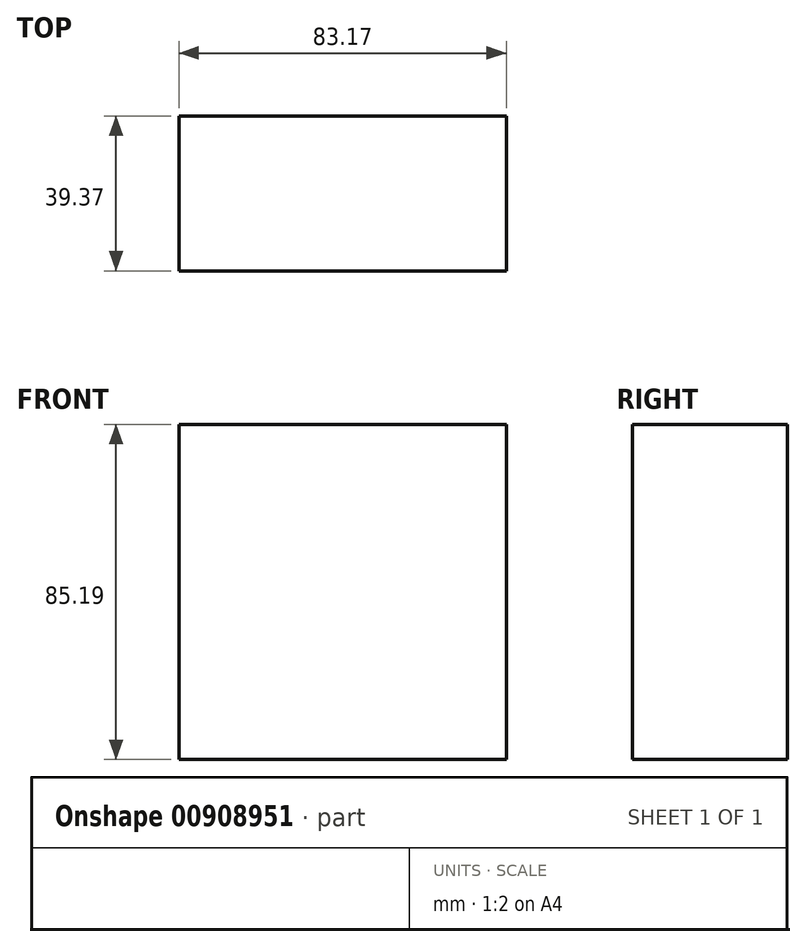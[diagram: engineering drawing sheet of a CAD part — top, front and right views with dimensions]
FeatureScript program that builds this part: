
annotation { "Feature Type Name" : "Feature", "Feature Type Description" : "" }
export const myFeature = defineFeature(function(context is Context, id is Id, definition is map)
    precondition{}
    {
        {
            var Q0;
            Q0=qCreatedBy(makeId("Front.planeOp"),FACE);
            var sketch = newSketch(context, id + "F0", { "sketchPlane" : qUnion([Q0])});
            skLineSegment(sketch, "E0.bottom", {"start": v(-42.1, 43.48) * mm, "end": v(41.08, 43.48) * mm});
            skLineSegment(sketch, "E0.top", {"start": v(-42.1, -41.71) * mm, "end": v(41.08, -41.71) * mm});
            skLineSegment(sketch, "E0.left", {"start": v(-42.1, 43.48) * mm, "end": v(-42.1, -41.71) * mm});
            skLineSegment(sketch, "E0.right", {"start": v(41.08, 43.48) * mm, "end": v(41.08, -41.71) * mm});
            skSolve(sketch);
        }
        {
            var Q0;
            Q0 = qSketchRegion(id + "F0", true);
            var Q1;
            Q1=makeQuery(id+"F0.imprint","IMPRINT",FACE,{"disambiguationData":[TD([[makeQuery(id+"F0.imprint","IMPRINT",EDGE,{"derivedFrom":sQuery(id+"F0.wireOp",EDGE,"E0.bottom")}),-1.0]])]});
            extrude(context, id + "F1", {"entities" : qUnion([Q0, Q1]), "depth" : 39.37 * mm, "offsetDistance" : 25.4 * mm});
        }
    });
